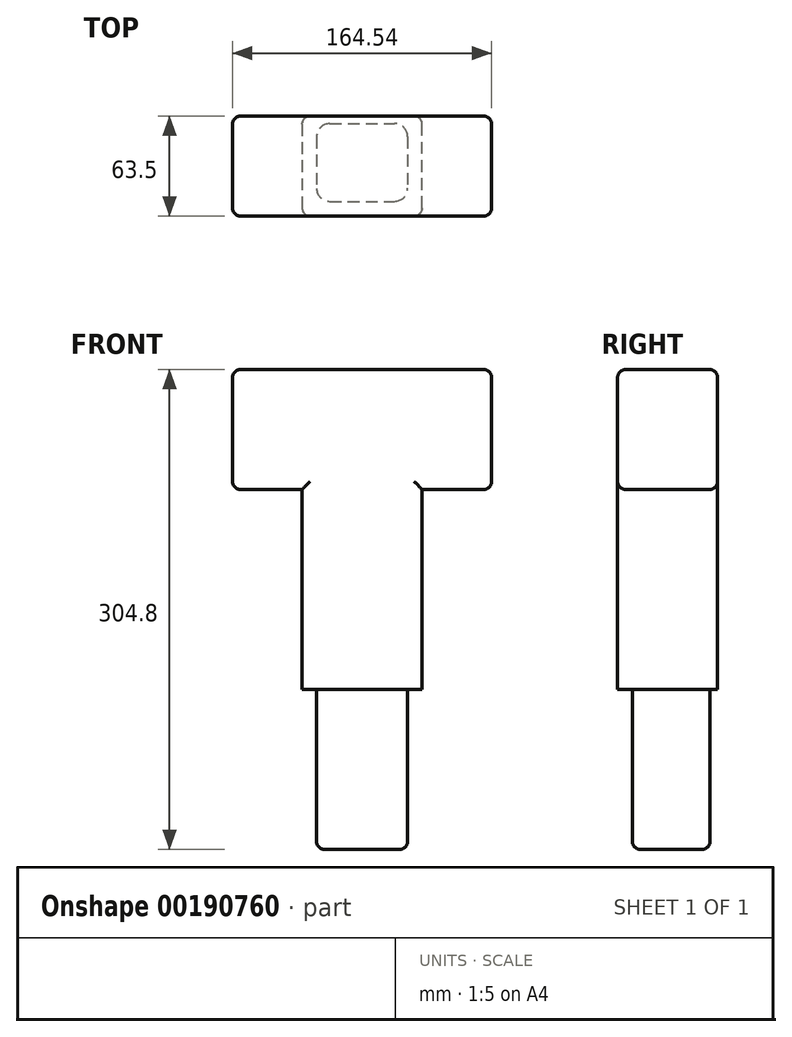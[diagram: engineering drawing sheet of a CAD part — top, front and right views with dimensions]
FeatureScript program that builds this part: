
annotation { "Feature Type Name" : "Feature", "Feature Type Description" : "" }
export const myFeature = defineFeature(function(context is Context, id is Id, definition is map)
    precondition{}
    {
        {
            var Q0;
            Q0=qCreatedBy(makeId("Front.planeOp"),FACE);
            var sketch = newSketch(context, id + "F0", { "sketchPlane" : qUnion([Q0])});
            skLineSegment(sketch, "E0.bottom", {"start": v(-38.1, -101.6) * mm, "end": v(38.1, -101.6) * mm});
            skLineSegment(sketch, "E0.top", {"start": v(-38.1, 101.6) * mm, "end": v(38.1, 101.6) * mm});
            skLineSegment(sketch, "E0.left", {"start": v(-38.1, -101.6) * mm, "end": v(-38.1, 101.6) * mm});
            skLineSegment(sketch, "E0.right", {"start": v(38.1, -101.6) * mm, "end": v(38.1, 101.6) * mm});
            skPoint(sketch, "E0.middle", {"position": v(0, 0) * mm});
            skSolve(sketch);
        }
        {
            var Q0;
            Q0 = qSketchRegion(id + "F0", true);
            extrude(context, id + "F1", {"entities" : qUnion([Q0]), "depth" : 63.5 * mm});
        }
        {
            var Q0;
            Q0=makeQuery(id+"F1.opExtrude","SWEPT_FACE",FACE,{"disambiguationData":[OSD([sQuery(id+"F0.wireOp",EDGE,"E0.bottom")])]});
            var sketch = newSketch(context, id + "F2", { "sketchPlane" : qUnion([Q0])});
            skLineSegment(sketch, "E1.bottom", {"start": v(-28.93, 4.77) * mm, "end": v(28.93, 4.77) * mm});
            skLineSegment(sketch, "E1.top", {"start": v(-28.93, 54.16) * mm, "end": v(28.93, 54.16) * mm});
            skLineSegment(sketch, "E1.left", {"start": v(-28.93, 4.77) * mm, "end": v(-28.93, 54.16) * mm});
            skLineSegment(sketch, "E1.right", {"start": v(28.93, 4.77) * mm, "end": v(28.93, 54.16) * mm});
            skPoint(sketch, "E1.middle", {"position": v(0, 29.47) * mm});
            skSolve(sketch);
        }
        {
            var Q0;
            Q0 = qSketchRegion(id + "F2", true);
            extrude(context, id + "F3", {"entities" : qUnion([Q0]), "operationType" : NewBodyOperationType.ADD, "depth" : 101.6 * mm});
        }
        {
            var Q0;
            Q0=makeQuery(id+"F3.opExtrude","SWEPT_EDGE",EDGE,{"disambiguationData":[OSD([sQuery(id+"F2.wireOp",EDGE,"E1.top"),sQuery(id+"F2.wireOp",EDGE,"E1.left")])]});
            fillet(context, id + "F4", {"entities" : qUnion([Q0]), "radius" : 8.25 * mm, "tangentPropagation" : true, "allowEdgeOverflow" : false});
        }
        {
            var Q0;
            Q0=makeQuery(id+"F3.opExtrude","SWEPT_EDGE",EDGE,{"disambiguationData":[OSD([sQuery(id+"F2.wireOp",EDGE,"E1.top"),sQuery(id+"F2.wireOp",EDGE,"E1.right")])]});
            var Q1;
            Q1=makeQuery(id+"F3.opExtrude","SWEPT_EDGE",EDGE,{"disambiguationData":[OSD([sQuery(id+"F2.wireOp",EDGE,"E1.bottom"),sQuery(id+"F2.wireOp",EDGE,"E1.right")])]});
            var Q2;
            Q2=makeQuery(id+"F3.opExtrude","SWEPT_EDGE",EDGE,{"disambiguationData":[OSD([sQuery(id+"F2.wireOp",EDGE,"E1.bottom"),sQuery(id+"F2.wireOp",EDGE,"E1.left")])]});
            fillet(context, id + "F5", {"entities" : qUnion([Q0, Q1, Q2]), "radius" : 8.33 * mm, "tangentPropagation" : true, "allowEdgeOverflow" : false});
        }
        {
            var Q0;
            Q0=makeQuery(id+"F3.opExtrude","CAP_EDGE",EDGE,{"disambiguationData":[OSD([sQuery(id+"F2.wireOp",EDGE,"E1.right")])],"isStart":false});
            var Q1;
            {var subQ0=sQuery(id+"F2.wireOp",EDGE,"E1.right");var subQ1=sQuery(id+"F2.wireOp",EDGE,"E1.top");Q1=makeQuery(id+"F5.opFillet","BLEND_EDGE",EDGE,{"blendedFrom":[makeQuery(id+"F3.opExtrude","SWEPT_EDGE",EDGE,{"disambiguationData":[OSD([subQ1,subQ0])]}),makeQuery(id+"F3.opExtrude","CAP_FACE",FACE,{"disambiguationData":[OSD([sQuery(id+"F2.wireOp",EDGE,"E1.bottom"),subQ1,sQuery(id+"F2.wireOp",EDGE,"E1.left"),subQ0])],"isStart":false})],"blendedInto":[makeQuery(id+"F3.opExtrude","CAP_FACE",FACE,{"disambiguationData":[OSD([sQuery(id+"F2.wireOp",EDGE,"E1.bottom"),subQ1,sQuery(id+"F2.wireOp",EDGE,"E1.left"),subQ0])],"isStart":false})]});}
            var Q2;
            {var subQ0=sQuery(id+"F2.wireOp",EDGE,"E1.right");var subQ1=sQuery(id+"F2.wireOp",EDGE,"E1.bottom");Q2=makeQuery(id+"F5.opFillet","BLEND_EDGE",EDGE,{"blendedFrom":[makeQuery(id+"F3.opExtrude","SWEPT_EDGE",EDGE,{"disambiguationData":[OSD([subQ1,subQ0])]}),makeQuery(id+"F3.opExtrude","CAP_FACE",FACE,{"disambiguationData":[OSD([subQ1,sQuery(id+"F2.wireOp",EDGE,"E1.top"),sQuery(id+"F2.wireOp",EDGE,"E1.left"),subQ0])],"isStart":false})],"blendedInto":[makeQuery(id+"F3.opExtrude","CAP_FACE",FACE,{"disambiguationData":[OSD([subQ1,sQuery(id+"F2.wireOp",EDGE,"E1.top"),sQuery(id+"F2.wireOp",EDGE,"E1.left"),subQ0])],"isStart":false})]});}
            var Q3;
            Q3=makeQuery(id+"F3.opExtrude","CAP_EDGE",EDGE,{"disambiguationData":[OSD([sQuery(id+"F2.wireOp",EDGE,"E1.bottom")])],"isStart":false});
            var Q4;
            Q4=makeQuery(id+"F3.opExtrude","CAP_EDGE",EDGE,{"disambiguationData":[OSD([sQuery(id+"F2.wireOp",EDGE,"E1.top")])],"isStart":false});
            var Q5;
            {var subQ0=sQuery(id+"F2.wireOp",EDGE,"E1.left");var subQ1=sQuery(id+"F2.wireOp",EDGE,"E1.top");Q5=makeQuery(id+"F4.opFillet","BLEND_EDGE",EDGE,{"blendedFrom":[makeQuery(id+"F3.opExtrude","SWEPT_EDGE",EDGE,{"disambiguationData":[OSD([subQ1,subQ0])]}),makeQuery(id+"F3.opExtrude","CAP_FACE",FACE,{"disambiguationData":[OSD([sQuery(id+"F2.wireOp",EDGE,"E1.bottom"),subQ1,subQ0,sQuery(id+"F2.wireOp",EDGE,"E1.right")])],"isStart":false})],"blendedInto":[makeQuery(id+"F3.opExtrude","CAP_FACE",FACE,{"disambiguationData":[OSD([sQuery(id+"F2.wireOp",EDGE,"E1.bottom"),subQ1,subQ0,sQuery(id+"F2.wireOp",EDGE,"E1.right")])],"isStart":false})]});}
            var Q6;
            Q6=makeQuery(id+"F3.opExtrude","CAP_EDGE",EDGE,{"disambiguationData":[OSD([sQuery(id+"F2.wireOp",EDGE,"E1.left")])],"isStart":false});
            var Q7;
            {var subQ0=sQuery(id+"F2.wireOp",EDGE,"E1.left");var subQ1=sQuery(id+"F2.wireOp",EDGE,"E1.bottom");Q7=makeQuery(id+"F5.opFillet","BLEND_EDGE",EDGE,{"blendedFrom":[makeQuery(id+"F3.opExtrude","SWEPT_EDGE",EDGE,{"disambiguationData":[OSD([subQ1,subQ0])]}),makeQuery(id+"F3.opExtrude","CAP_FACE",FACE,{"disambiguationData":[OSD([subQ1,sQuery(id+"F2.wireOp",EDGE,"E1.top"),subQ0,sQuery(id+"F2.wireOp",EDGE,"E1.right")])],"isStart":false})],"blendedInto":[makeQuery(id+"F3.opExtrude","CAP_FACE",FACE,{"disambiguationData":[OSD([subQ1,sQuery(id+"F2.wireOp",EDGE,"E1.top"),subQ0,sQuery(id+"F2.wireOp",EDGE,"E1.right")])],"isStart":false})]});}
            fillet(context, id + "F6", {"entities" : qUnion([Q0, Q1, Q2, Q3, Q4, Q5, Q6, Q7]), "radius" : 5.08 * mm, "tangentPropagation" : true, "allowEdgeOverflow" : false});
        }
        {
            var Q0;
            Q0=makeQuery(id+"F1.opExtrude","CAP_FACE",FACE,{"disambiguationData":[OSD([sQuery(id+"F0.wireOp",EDGE,"E0.bottom"),sQuery(id+"F0.wireOp",EDGE,"E0.top"),sQuery(id+"F0.wireOp",EDGE,"E0.left"),sQuery(id+"F0.wireOp",EDGE,"E0.right")])],"isStart":false});
            var sketch = newSketch(context, id + "F7", { "sketchPlane" : qUnion([Q0])});
            skLineSegment(sketch, "E2.bottom", {"start": v(-82.27, 101.6) * mm, "end": v(82.27, 101.6) * mm});
            skLineSegment(sketch, "E2.top", {"start": v(-82.27, 25.4) * mm, "end": v(82.27, 25.4) * mm});
            skLineSegment(sketch, "E2.left", {"start": v(-82.27, 101.6) * mm, "end": v(-82.27, 25.4) * mm});
            skLineSegment(sketch, "E2.right", {"start": v(82.27, 101.6) * mm, "end": v(82.27, 25.4) * mm});
            skPoint(sketch, "E3", {"position": v(0, 101.6) * mm});
            skPoint(sketch, "E4", {"position": v(-38.1, 101.6) * mm});
            skPoint(sketch, "E5", {"position": v(38.1, 101.6) * mm});
            skSolve(sketch);
        }
        {
            var Q0;
            Q0 = qSketchRegion(id + "F7", true);
            extrude(context, id + "F8", {"entities" : qUnion([Q0]), "operationType" : NewBodyOperationType.ADD, "oppositeDirection" : true, "depth" : 63.5 * mm});
        }
        {
            var Q0;
            Q0=makeQuery(id+"F8.boolean.opBoolean","MERGE",EDGE,{"derivedFrom":[makeQuery(id+"F1.opExtrude","CAP_EDGE",EDGE,{"disambiguationData":[OSD([sQuery(id+"F0.wireOp",EDGE,"E0.top")])],"isStart":false}),makeQuery(id+"F8.opExtrude","CAP_EDGE",EDGE,{"disambiguationData":[OSD([sQuery(id+"F7.wireOp",EDGE,"E2.bottom")])],"isStart":true})]});
            var Q1;
            Q1=makeQuery(id+"F8.boolean.opBoolean","MERGE",EDGE,{"derivedFrom":[makeQuery(id+"F1.opExtrude","CAP_EDGE",EDGE,{"disambiguationData":[OSD([sQuery(id+"F0.wireOp",EDGE,"E0.top")])],"isStart":true}),makeQuery(id+"F8.opExtrude","CAP_EDGE",EDGE,{"disambiguationData":[OSD([sQuery(id+"F7.wireOp",EDGE,"E2.bottom")])],"isStart":false})]});
            var Q2;
            {var subQ0=sQuery(id+"F7.wireOp",EDGE,"E2.top");var subQ2=sQuery(id+"F0.wireOp",EDGE,"E0.left");Q2=makeQuery(id+"F8.boolean.opBoolean","SPLIT",EDGE,{"disambiguationData":[TD([makeQuery(id+"F1.opExtrude","SWEPT_FACE",FACE,{"disambiguationData":[OSD([subQ2])]})])],"derivedFrom":makeQuery(id+"F8.opExtrude","CAP_EDGE",EDGE,{"disambiguationData":[OSD([subQ0])],"isStart":false})});}
            var Q3;
            {var subQ0=sQuery(id+"F7.wireOp",EDGE,"E2.top");var subQ2=sQuery(id+"F0.wireOp",EDGE,"E0.right");Q3=makeQuery(id+"F8.boolean.opBoolean","SPLIT",EDGE,{"disambiguationData":[TD([makeQuery(id+"F1.opExtrude","SWEPT_FACE",FACE,{"disambiguationData":[OSD([subQ2])]})])],"derivedFrom":makeQuery(id+"F8.opExtrude","CAP_EDGE",EDGE,{"disambiguationData":[OSD([subQ0])],"isStart":false})});}
            var Q4;
            {var subQ0=sQuery(id+"F7.wireOp",EDGE,"E2.top");var subQ2=sQuery(id+"F0.wireOp",EDGE,"E0.left");Q4=makeQuery(id+"F8.boolean.opBoolean","SPLIT",EDGE,{"disambiguationData":[TD([makeQuery(id+"F1.opExtrude","SWEPT_FACE",FACE,{"disambiguationData":[OSD([subQ2])]})])],"derivedFrom":makeQuery(id+"F8.opExtrude","CAP_EDGE",EDGE,{"disambiguationData":[OSD([subQ0])],"isStart":true})});}
            var Q5;
            {var subQ0=sQuery(id+"F7.wireOp",EDGE,"E2.top");var subQ2=sQuery(id+"F0.wireOp",EDGE,"E0.right");Q5=makeQuery(id+"F8.boolean.opBoolean","SPLIT",EDGE,{"disambiguationData":[TD([makeQuery(id+"F1.opExtrude","SWEPT_FACE",FACE,{"disambiguationData":[OSD([subQ2])]})])],"derivedFrom":makeQuery(id+"F8.opExtrude","CAP_EDGE",EDGE,{"disambiguationData":[OSD([subQ0])],"isStart":true})});}
            var Q6;
            Q6=makeQuery(id+"F8.opExtrude","SWEPT_FACE",FACE,{"disambiguationData":[OSD([sQuery(id+"F7.wireOp",EDGE,"E2.right")])]});
            var Q7;
            Q7=makeQuery(id+"F8.opExtrude","SWEPT_FACE",FACE,{"disambiguationData":[OSD([sQuery(id+"F7.wireOp",EDGE,"E2.left")])]});
            var Q8;
            Q8=makeQuery(id+"F1.opExtrude","CAP_EDGE",EDGE,{"disambiguationData":[OSD([sQuery(id+"F0.wireOp",EDGE,"E0.left")])],"isStart":false});
            var Q9;
            Q9=makeQuery(id+"F1.opExtrude","CAP_EDGE",EDGE,{"disambiguationData":[OSD([sQuery(id+"F0.wireOp",EDGE,"E0.right")])],"isStart":false});
            var Q10;
            Q10=makeQuery(id+"F1.opExtrude","CAP_EDGE",EDGE,{"disambiguationData":[OSD([sQuery(id+"F0.wireOp",EDGE,"E0.left")])],"isStart":true});
            var Q11;
            Q11=makeQuery(id+"F1.opExtrude","CAP_EDGE",EDGE,{"disambiguationData":[OSD([sQuery(id+"F0.wireOp",EDGE,"E0.right")])],"isStart":true});
            fillet(context, id + "F9", {"entities" : qUnion([Q0, Q1, Q2, Q3, Q4, Q5, Q6, Q7, Q8, Q9, Q10, Q11]), "radius" : 5.08 * mm, "tangentPropagation" : true, "allowEdgeOverflow" : false});
        }
    });
